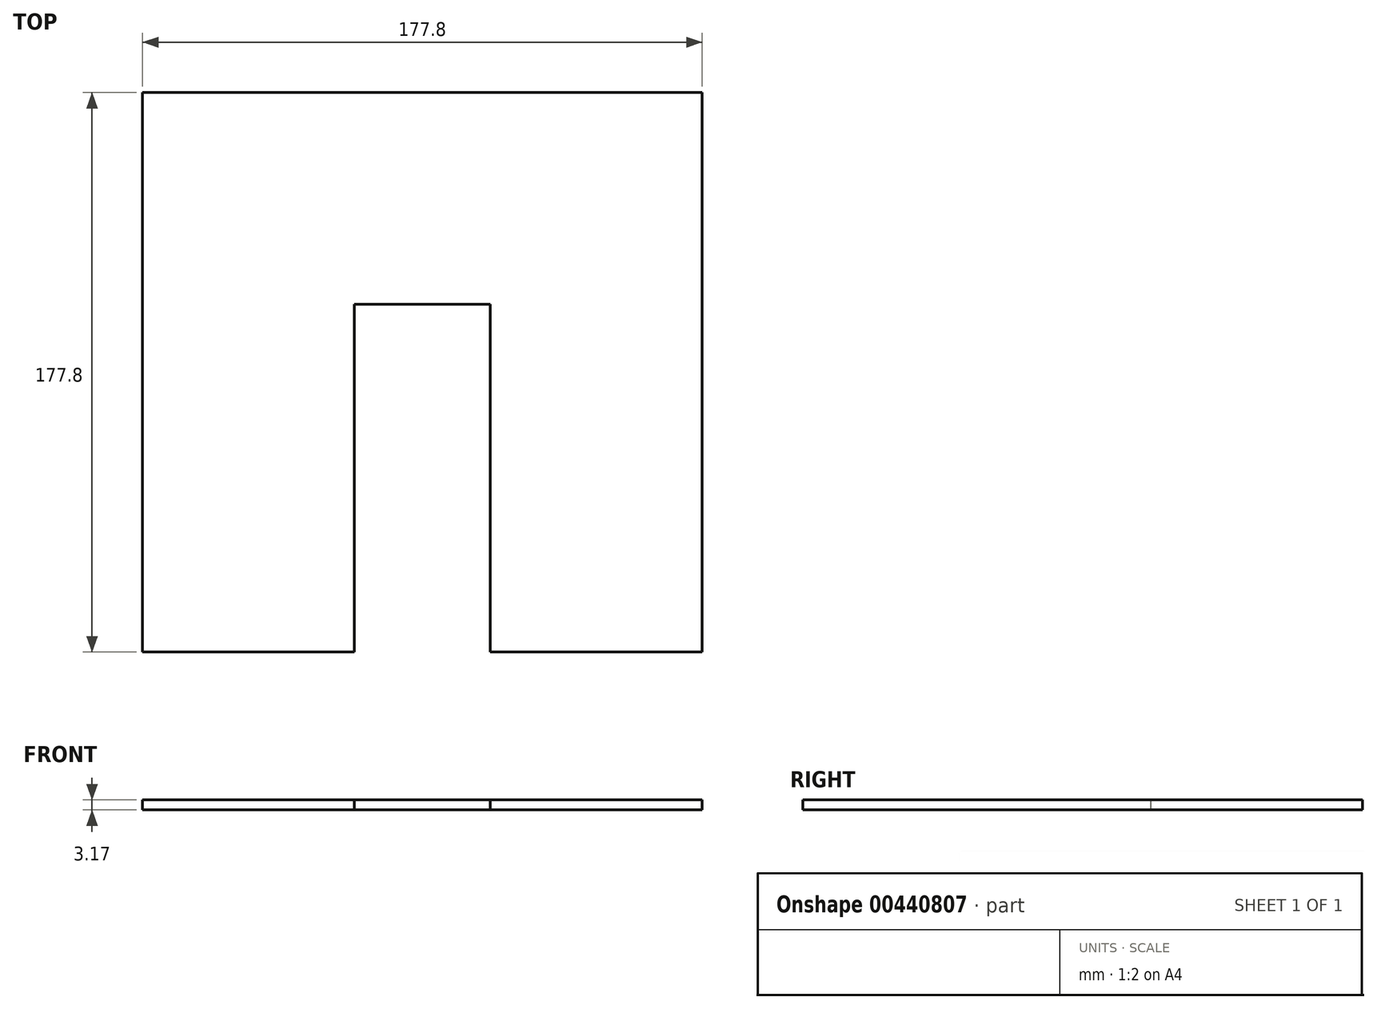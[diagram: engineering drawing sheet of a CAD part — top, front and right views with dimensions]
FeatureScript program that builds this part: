
annotation { "Feature Type Name" : "Feature", "Feature Type Description" : "" }
export const myFeature = defineFeature(function(context is Context, id is Id, definition is map)
    precondition{}
    {
        {
            var Q0;
            Q0=qCreatedBy(makeId("Top.planeOp"),FACE);
            var sketch = newSketch(context, id + "F0", { "sketchPlane" : qUnion([Q0])});
            skLineSegment(sketch, "E0.bottom", {"start": v(88.9, 88.9) * mm, "end": v(-88.9, 88.9) * mm});
            skLineSegment(sketch, "E0.top", {"start": v(88.9, -88.9) * mm, "end": v(-88.9, -88.9) * mm});
            skLineSegment(sketch, "E0.left", {"start": v(88.9, 88.9) * mm, "end": v(88.9, -88.9) * mm});
            skLineSegment(sketch, "E0.right", {"start": v(-88.9, 88.9) * mm, "end": v(-88.9, -88.9) * mm});
            skLineSegment(sketch, "E1.bottom", {"start": v(21.59, 21.6) * mm, "end": v(-21.6, 21.6) * mm});
            skLineSegment(sketch, "E1.top", {"start": v(21.6, -21.6) * mm, "end": v(-21.59, -21.6) * mm});
            skLineSegment(sketch, "E1.left", {"start": v(21.59, 21.6) * mm, "end": v(21.6, -21.6) * mm});
            skLineSegment(sketch, "E1.right", {"start": v(-21.6, 21.6) * mm, "end": v(-21.59, -21.6) * mm});
            skPoint(sketch, "E1.middle", {"position": v(0, 0) * mm});
            skLineSegment(sketch, "E2.bottom", {"start": v(-21.6, -21.6) * mm, "end": v(21.6, -21.6) * mm});
            skLineSegment(sketch, "E2.top", {"start": v(-21.6, -88.9) * mm, "end": v(21.6, -88.9) * mm});
            skLineSegment(sketch, "E2.left", {"start": v(-21.59, -21.6) * mm, "end": v(-21.59, -88.9) * mm});
            skLineSegment(sketch, "E2.right", {"start": v(21.6, -21.6) * mm, "end": v(21.6, -88.9) * mm});
            skSolve(sketch);
        }
        {
            var Q0;
            Q0=makeQuery(id+"F0.imprint","IMPRINT",FACE,{"disambiguationData":[TD([[makeQuery(id+"F0.imprint","IMPRINT",EDGE,{"derivedFrom":sQuery(id+"F0.wireOp",EDGE,"E0.bottom")}),1.0]])]});
            extrude(context, id + "F1", {"entities" : qUnion([Q0]), "depth" : 3.17 * mm});
        }
    });
